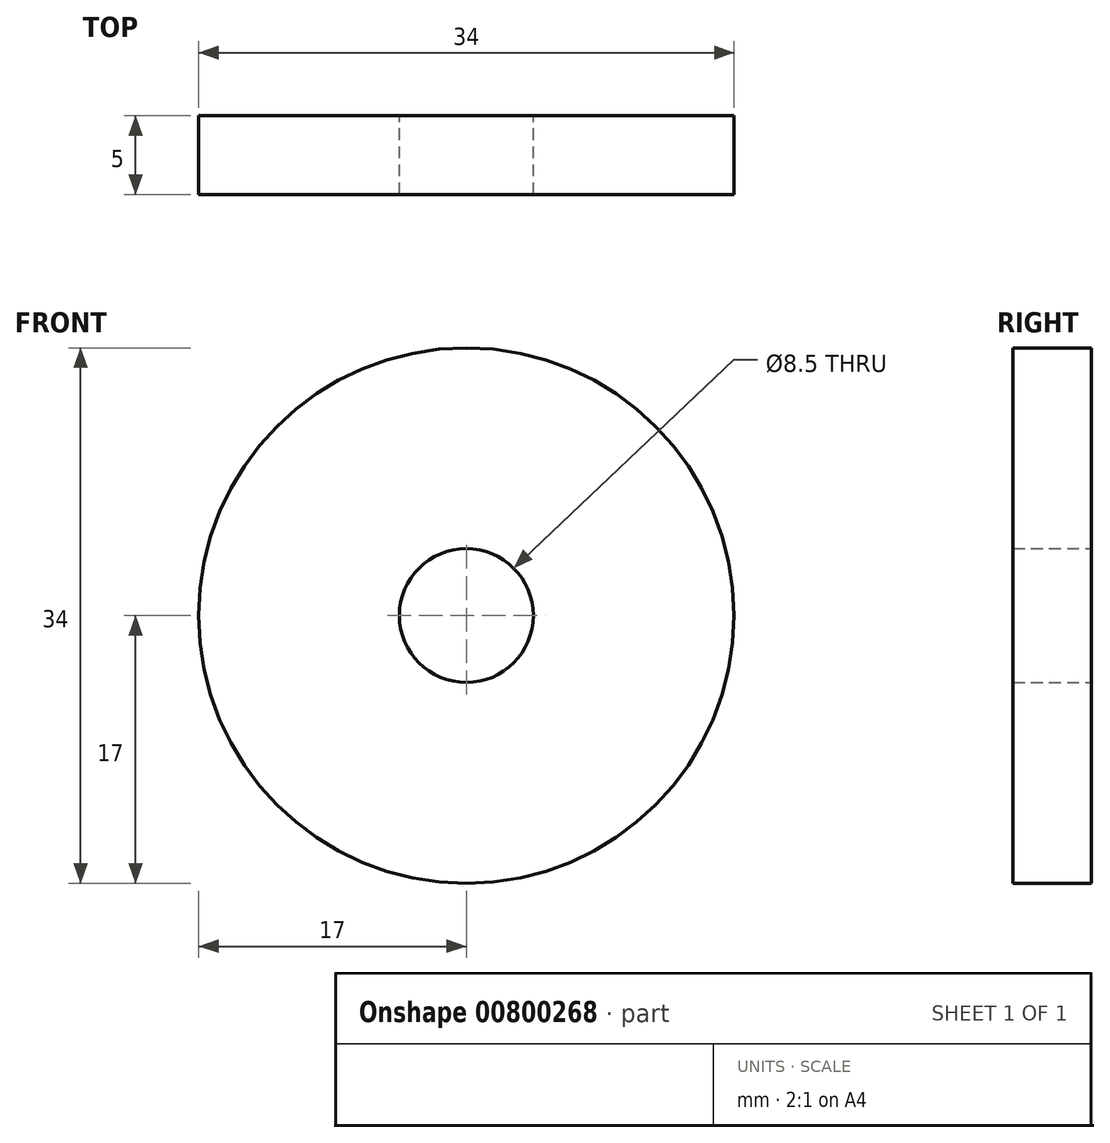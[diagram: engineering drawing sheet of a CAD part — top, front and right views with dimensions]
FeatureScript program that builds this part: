
annotation { "Feature Type Name" : "Feature", "Feature Type Description" : "" }
export const myFeature = defineFeature(function(context is Context, id is Id, definition is map)
    precondition{}
    {
        {
            var Q0;
            Q0=qCreatedBy(makeId("Front.planeOp"),FACE);
            var sketch = newSketch(context, id + "F0", { "sketchPlane" : qUnion([Q0])});
            skCircle(sketch, "E0", {"center": v(0, 0) * mm, "radius": 17 * mm});
            skCircle(sketch, "E1", {"center": v(0, 0) * mm, "radius": 4.25 * mm});
            skSolve(sketch);
        }
        {
            var Q0;
            Q0=qSketchRegion(id+"F0",true);
            extrude(context, id + "F1", {"entities" : qUnion([Q0]), "depth" : 5 * mm, "offsetDistance" : 25 * mm});
        }
    });
